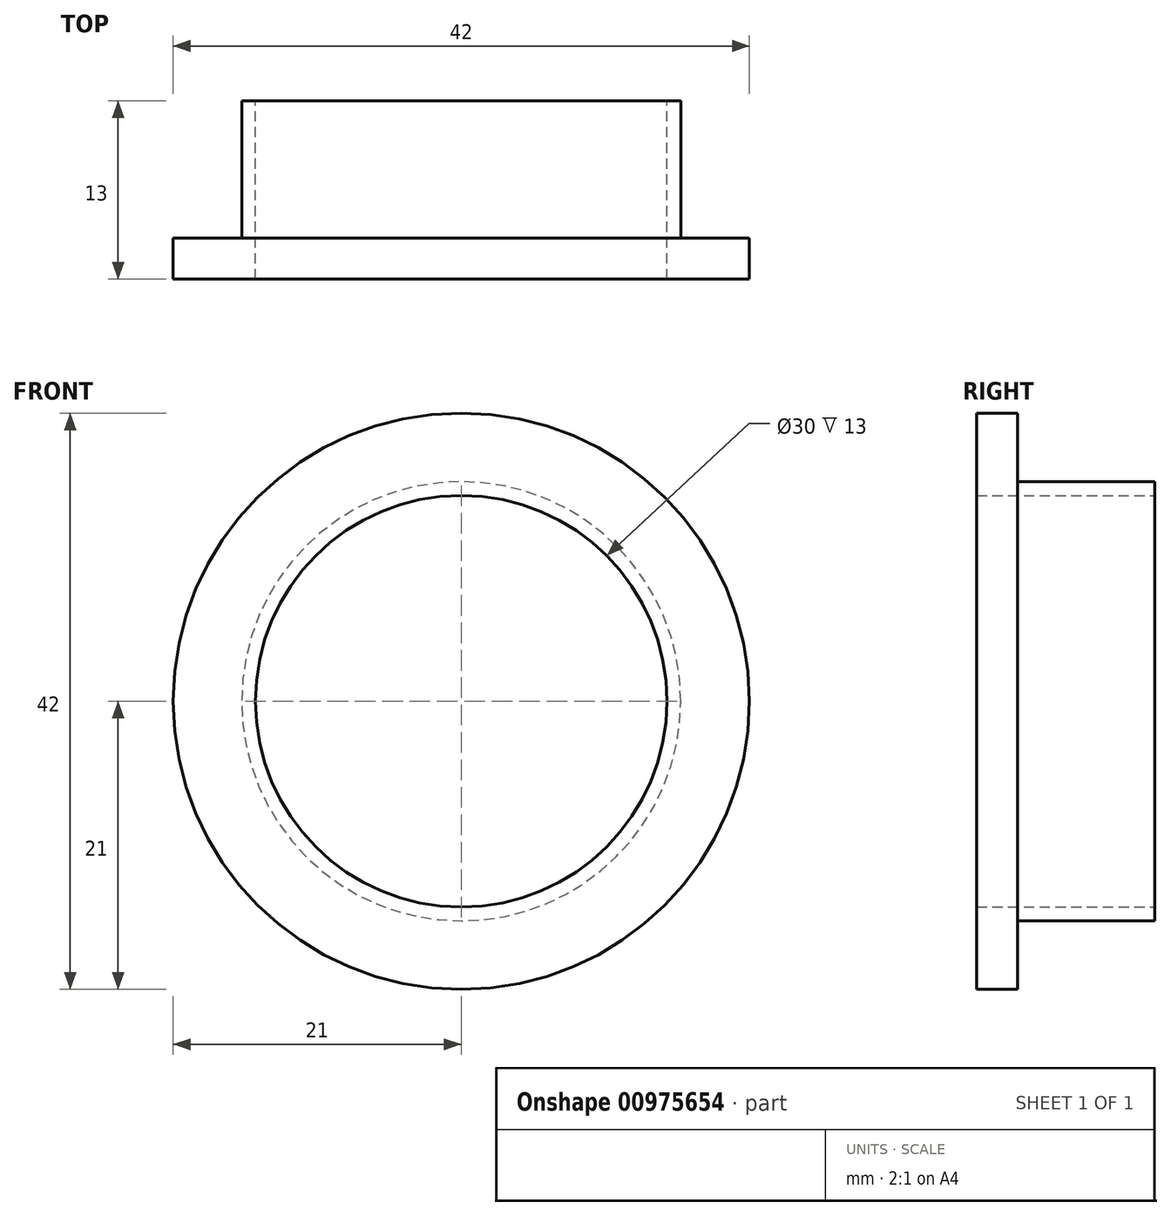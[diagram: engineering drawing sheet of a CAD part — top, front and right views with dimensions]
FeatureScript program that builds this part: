
annotation { "Feature Type Name" : "Feature", "Feature Type Description" : "" }
export const myFeature = defineFeature(function(context is Context, id is Id, definition is map)
    precondition{}
    {
        {
            var Q0;
            Q0=qCreatedBy(makeId("Front.planeOp"),FACE);
            var sketch = newSketch(context, id + "F0", { "sketchPlane" : qUnion([Q0])});
            skCircle(sketch, "E0", {"center": v(0, 0) * mm, "radius": 15 * mm});
            skCircle(sketch, "E1.0", {"center": v(0, 0) * mm, "radius": 16 * mm});
            skSolve(sketch);
        }
        {
            var Q0;
            Q0=qSketchRegion(id+"F0",true);
            extrude(context, id + "F1", {"entities" : qUnion([Q0]), "depth" : 10 * mm, "offsetDistance" : 25 * mm});
        }
        {
            var Q0;
            Q0=makeQuery(id+"F1.opExtrude","CAP_FACE",FACE,{"disambiguationData":[OSD([sQuery(id+"F0.wireOp",EDGE,"E0"),sQuery(id+"F0.wireOp",EDGE,"E1.0")])],"isStart":false});
            cPlane(context, id + "F2", {"entities" : qUnion([Q0]), "cplaneType" : CPlaneType.OFFSET, "offset" : 0 * mm, "width" : 150 * mm, "height" : 150 * mm});
        }
        {
            var Q0;
            Q0=qCreatedBy(id+"F2.planeOp",FACE);
            var sketch = newSketch(context, id + "F3", { "sketchPlane" : qUnion([Q0])});
            skCircle(sketch, "E2.0", {"center": v(0, 0) * mm, "radius": 15 * mm});
            skCircle(sketch, "E3.0", {"center": v(0, 0) * mm, "radius": 21 * mm});
            skSolve(sketch);
        }
        {
            var Q0;
            Q0=qSketchRegion(id+"F3",true);
            extrude(context, id + "F4", {"entities" : qUnion([Q0]), "operationType" : NewBodyOperationType.ADD, "depth" : 3 * mm, "offsetDistance" : 25 * mm});
        }
    });
